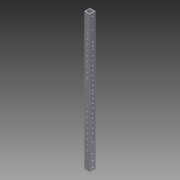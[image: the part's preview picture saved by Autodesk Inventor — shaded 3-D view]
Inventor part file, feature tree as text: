
AUTODESK INVENTOR PART (.ipt)
format: ipt  version: 2013 (Build 170138000, 138)  size: 270,336 bytes
history: native  units: in
note: dims shown in document units (in); Inventor stores cm internally (conversion verified against a paired STEP export)
features: extrude x4, sketch x4
ambient origin geometry x8: Origin, YZ Plane, XZ Plane, XY Plane, X Axis, Y Axis, Z Axis, Center Point
bodies: Solid1 (feature_tree)
feature tree (8):
  extrude  "Extrusion1"  Depth=1.0in
  extrude  "Extrusion2"  Depth=24.0in TaperAngle=0.0deg
  extrude  "Extrusion3"  Depth=0.26in
  extrude  "Extrusion4"  Depth=11.0236in
  sketch  "Sketch1"  dims[d0=1.0in d1=1.0in]
  sketch  "Sketch2"  dims[d2=0.125in d3=24.0in d4=0.0in]
  sketch  "Sketch3"  dims[d5=0.55in d6=0.26in]
  sketch  "Sketch4"  dims[d7=24.0in d8=11.0236in d10=0.8481in d11=0.3937in d13=1.0in d15=1.0in d16=0.0in d17=1.75in d18=2.0in d19=1.75in d20=1.75in d21=0.26in d22=0.26in d23=0.26in d24=0.26in d25=0.26in d26=0.26in d27=0.26in d28=0.26in d29=1.0in d30=0.0in d31=2.0in d32=0.26in d33=0.26in d40=0.5in d41=0.26in d42=0.5in d43=0.26in d46=0.75in d47=0.75in d48=0.26in d49=0.26in d50=1.0in d51=0.0in d52=0.26in d53=5.5in d64=1.0in d65=0.26in d66=0.55in d67=24.0in d68=11.0236in d70=0.8481in d71=0.3937in d73=1.0in d76=0.375in d77=0.375in d85=0.5in d86=2.7559in d88=0.75in d89=0.3937in d91=1.0in d93=2.3622in d95=0.75in d96=0.3937in d98=1.0in d100=0.75in d101=0.75in]
